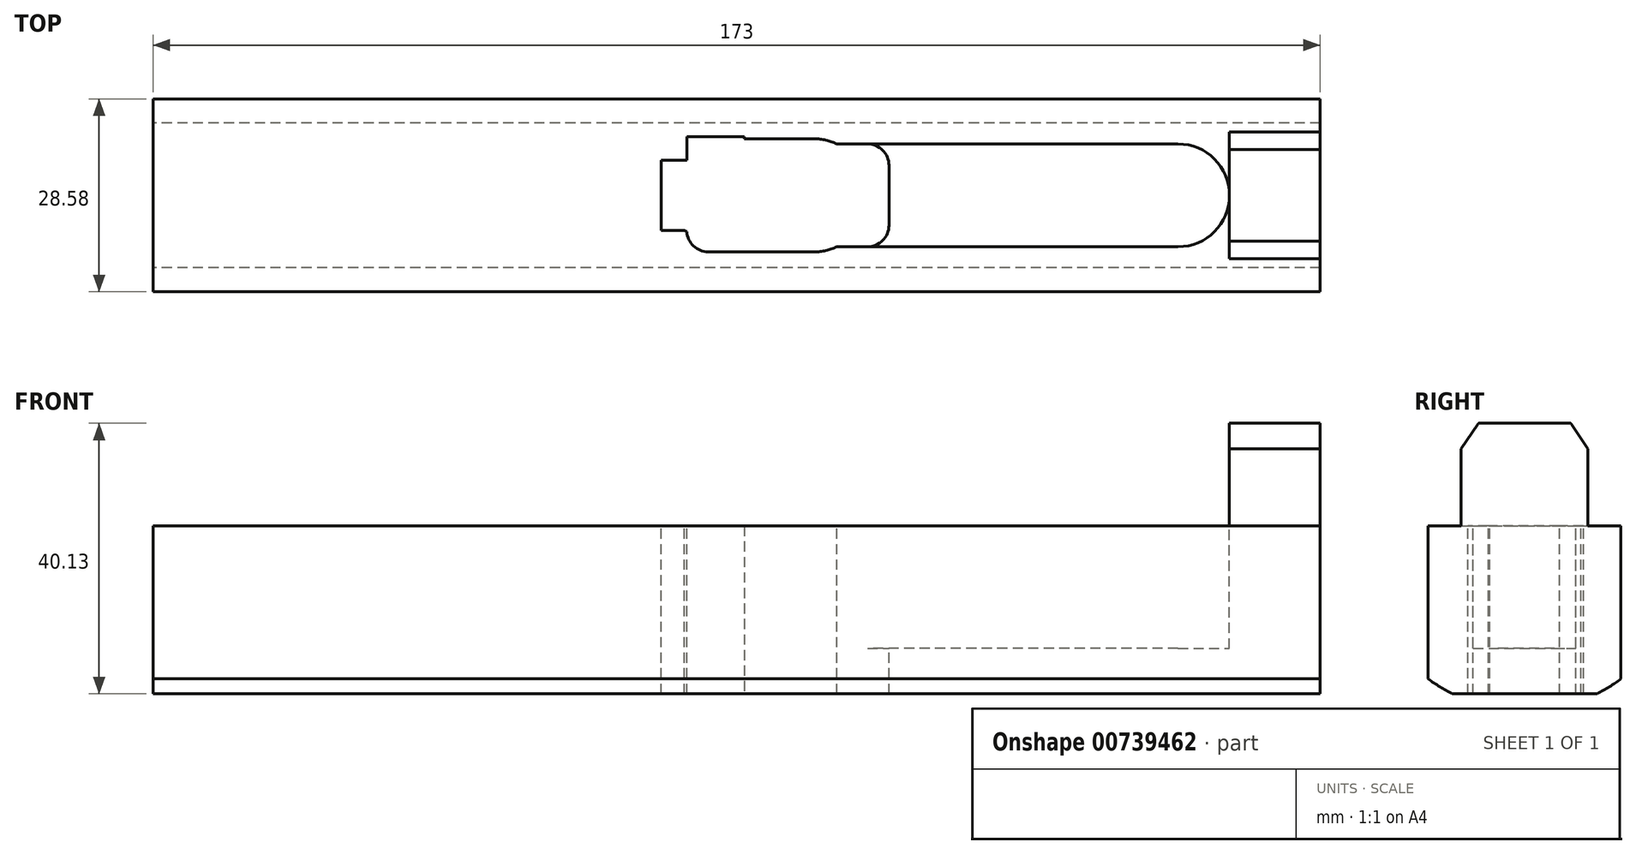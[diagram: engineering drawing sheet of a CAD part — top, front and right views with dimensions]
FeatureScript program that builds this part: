
annotation { "Feature Type Name" : "Feature", "Feature Type Description" : "" }
export const myFeature = defineFeature(function(context is Context, id is Id, definition is map)
    precondition{}
    {
        {
            var Q0;
            Q0=qCreatedBy(makeId("Right.planeOp"),FACE);
            var sketch = newSketch(context, id + "F0", { "sketchPlane" : qUnion([Q0])});
            skLineSegment(sketch, "E0", {"start": v(16, 0) * mm, "end": v(16, 22.54) * mm});
            skLineSegment(sketch, "E1", {"start": v(15.74, 23.38) * mm, "end": v(6.95, 36.34) * mm});
            skLineSegment(sketch, "E2", {"start": v(5.7, 37) * mm, "end": v(-5.7, 37) * mm});
            skLineSegment(sketch, "E3", {"start": v(-6.95, 36.34) * mm, "end": v(-15.74, 23.38) * mm});
            skLineSegment(sketch, "E4", {"start": v(-16, 22.54) * mm, "end": v(-16, 0) * mm});
            skLineSegment(sketch, "E5", {"start": v(-25.86, -6.2) * mm, "end": v(32.15, -6.2) * mm, "construction": true});
            skArc(sketch, "E6", {"start": v(-16, 0) * mm, "mid": v(0, -6.2) * mm, "end": v(16, 0) * mm});
            skPoint(sketch, "E6.third.point", {"position": v(0, -6.2) * mm});
            skPoint(sketch, "E7.visualSharp", {"position": v(-6.5, 37) * mm});
            skArc(sketch, "E7.filletArc", {"start": v(-5.7, 37) * mm, "mid": v(-6.4, 36.83) * mm, "end": v(-6.95, 36.34) * mm});
            skPoint(sketch, "E8.visualSharp", {"position": v(6.5, 37) * mm});
            skArc(sketch, "E8.filletArc", {"start": v(6.95, 36.34) * mm, "mid": v(6.4, 36.83) * mm, "end": v(5.7, 37) * mm});
            skPoint(sketch, "E9.visualSharp", {"position": v(-16, 23) * mm});
            skArc(sketch, "E9.filletArc", {"start": v(-15.74, 23.38) * mm, "mid": v(-15.93, 22.98) * mm, "end": v(-16, 22.54) * mm});
            skPoint(sketch, "E10.visualSharp", {"position": v(16, 23) * mm});
            skArc(sketch, "E10.filletArc", {"start": v(16, 22.54) * mm, "mid": v(15.93, 22.98) * mm, "end": v(15.74, 23.38) * mm});
            skSolve(sketch);
        }
        {
            var Q0;
            Q0 = qSketchRegion(id + "F0", true);
            extrude(context, id + "F1", {"entities" : qUnion([Q0]), "depth" : 173 * mm, "offsetDistance" : 25.4 * mm});
        }
        {
            var Q0;
            Q0=makeQuery(id+"F1.opExtrude","CAP_FACE",FACE,{"disambiguationData":[OSD([sQuery(id+"F0.wireOp",EDGE,"E0"),sQuery(id+"F0.wireOp",EDGE,"E1"),sQuery(id+"F0.wireOp",EDGE,"E2"),sQuery(id+"F0.wireOp",EDGE,"E3"),sQuery(id+"F0.wireOp",EDGE,"E4"),sQuery(id+"F0.wireOp",EDGE,"E6"),sQuery(id+"F0.wireOp",EDGE,"E7.filletArc"),sQuery(id+"F0.wireOp",EDGE,"E8.filletArc"),sQuery(id+"F0.wireOp",EDGE,"E9.filletArc"),sQuery(id+"F0.wireOp",EDGE,"E10.filletArc")])],"isStart":true});
            var sketch = newSketch(context, id + "F2", { "sketchPlane" : qUnion([Q0])});
            skLineSegment(sketch, "E11", {"start": v(-9.4, 21.26) * mm, "end": v(-16, 21.26) * mm});
            skLineSegment(sketch, "E12", {"start": v(-16, 21.26) * mm, "end": v(-16, 39.2) * mm});
            skLineSegment(sketch, "E13", {"start": v(-16, 39.2) * mm, "end": v(16, 39.2) * mm});
            skLineSegment(sketch, "E14", {"start": v(-9.4, 21.26) * mm, "end": v(-9.4, 36.5) * mm});
            skLineSegment(sketch, "E15", {"start": v(-9.4, 36.5) * mm, "end": v(9.4, 36.5) * mm});
            skLineSegment(sketch, "E16", {"start": v(9.4, 36.5) * mm, "end": v(9.4, 21.26) * mm});
            skLineSegment(sketch, "E17", {"start": v(9.4, 21.26) * mm, "end": v(16, 21.26) * mm});
            skLineSegment(sketch, "E18", {"start": v(16, 21.26) * mm, "end": v(16, 39.2) * mm});
            skSolve(sketch);
        }
        {
            var Q0;
            Q0 = qSketchRegion(id + "F2", true);
            extrude(context, id + "F3", {"entities" : qUnion([Q0]), "operationType" : NewBodyOperationType.REMOVE, "endBound" : BoundingType.THROUGH_ALL, "oppositeDirection" : true, "depth" : 25 * mm, "offsetDistance" : 25 * mm});
        }
        {
            var Q0;
            Q0=makeQuery(id+"F1.opExtrude","CAP_FACE",FACE,{"disambiguationData":[OSD([sQuery(id+"F0.wireOp",EDGE,"E0"),sQuery(id+"F0.wireOp",EDGE,"E1"),sQuery(id+"F0.wireOp",EDGE,"E2"),sQuery(id+"F0.wireOp",EDGE,"E3"),sQuery(id+"F0.wireOp",EDGE,"E4"),sQuery(id+"F0.wireOp",EDGE,"E6"),sQuery(id+"F0.wireOp",EDGE,"E7.filletArc"),sQuery(id+"F0.wireOp",EDGE,"E8.filletArc"),sQuery(id+"F0.wireOp",EDGE,"E9.filletArc"),sQuery(id+"F0.wireOp",EDGE,"E10.filletArc")])],"isStart":true});
            var sketch = newSketch(context, id + "F4", { "sketchPlane" : qUnion([Q0])});
            skLineSegment(sketch, "E19", {"start": v(-16, 21.26) * mm, "end": v(-14.29, 21.26) * mm});
            skLineSegment(sketch, "E20", {"start": v(-14.29, 21.26) * mm, "end": v(-14.29, -3.63) * mm});
            skLineSegment(sketch, "E21", {"start": v(-14.29, -3.63) * mm, "end": v(14.29, -3.63) * mm});
            skLineSegment(sketch, "E22", {"start": v(14.29, -3.63) * mm, "end": v(14.29, 21.26) * mm});
            skLineSegment(sketch, "E23", {"start": v(14.29, 21.26) * mm, "end": v(16, 21.26) * mm});
            skLineSegment(sketch, "E24", {"start": v(16, 21.26) * mm, "end": v(16, -10.53) * mm});
            skLineSegment(sketch, "E25", {"start": v(16, -10.53) * mm, "end": v(-16, -10.53) * mm});
            skLineSegment(sketch, "E26", {"start": v(-16, 21.26) * mm, "end": v(-16, -10.53) * mm});
            skSolve(sketch);
        }
        {
            var Q0;
            Q0 = qSketchRegion(id + "F4", true);
            extrude(context, id + "F5", {"entities" : qUnion([Q0]), "operationType" : NewBodyOperationType.REMOVE, "endBound" : BoundingType.THROUGH_ALL, "oppositeDirection" : true, "depth" : 25 * mm, "offsetDistance" : 25 * mm});
        }
        {
            var Q0;
            Q0=makeQuery(id+"F3.boolean.opBoolean","COPY",FACE,{"derivedFrom":makeQuery(id+"F3.opExtrude","SWEPT_FACE",FACE,{"disambiguationData":[OSD([sQuery(id+"F2.wireOp",EDGE,"E14")])]})});
            var sketch = newSketch(context, id + "F6", { "sketchPlane" : qUnion([Q0])});
            skLineSegment(sketch, "E27.bottom", {"start": v(-159.54, 21.26) * mm, "end": v(0, 21.26) * mm});
            skLineSegment(sketch, "E27.top", {"start": v(-159.54, 36.5) * mm, "end": v(0, 36.5) * mm});
            skLineSegment(sketch, "E27.left", {"start": v(-159.54, 21.26) * mm, "end": v(-159.54, 36.5) * mm});
            skLineSegment(sketch, "E27.right", {"start": v(0, 21.26) * mm, "end": v(0, 36.5) * mm});
            skSolve(sketch);
        }
        {
            var Q0;
            Q0 = qSketchRegion(id + "F6", true);
            extrude(context, id + "F7", {"entities" : qUnion([Q0]), "operationType" : NewBodyOperationType.REMOVE, "endBound" : BoundingType.THROUGH_ALL, "oppositeDirection" : true, "depth" : 25 * mm, "offsetDistance" : 25 * mm});
        }
        {
            var Q0;
            Q0=makeQuery(id+"F7.boolean.opBoolean","MERGE",FACE,{"derivedFrom":[makeQuery(id+"F3.boolean.opBoolean","COPY",FACE,{"derivedFrom":makeQuery(id+"F3.opExtrude","SWEPT_FACE",FACE,{"disambiguationData":[OSD([sQuery(id+"F2.wireOp",EDGE,"E11")])]})}),makeQuery(id+"F3.boolean.opBoolean","COPY",FACE,{"derivedFrom":makeQuery(id+"F3.opExtrude","SWEPT_FACE",FACE,{"disambiguationData":[OSD([sQuery(id+"F2.wireOp",EDGE,"E17")])]})}),makeQuery(id+"F7.opExtrude","SWEPT_FACE",FACE,{"disambiguationData":[OSD([sQuery(id+"F6.wireOp",EDGE,"E27.bottom")])]})]});
            var sketch = newSketch(context, id + "F8", { "sketchPlane" : qUnion([Q0])});
            skArc(sketch, "E28", {"start": v(151.92, -7.62) * mm, "mid": v(159.54, 0) * mm, "end": v(151.92, 7.62) * mm});
            skLineSegment(sketch, "E29", {"start": v(151.92, 7.62) * mm, "end": v(85.98, 7.62) * mm});
            skLineSegment(sketch, "E30", {"start": v(151.92, -7.62) * mm, "end": v(85.98, -7.62) * mm});
            skArc(sketch, "E31", {"start": v(85.98, 7.62) * mm, "mid": v(78.36, 0) * mm, "end": v(85.98, -7.62) * mm});
            skSolve(sketch);
        }
        {
            var Q0;
            Q0 = qSketchRegion(id + "F8", true);
            extrude(context, id + "F9", {"entities" : qUnion([Q0]), "operationType" : NewBodyOperationType.REMOVE, "oppositeDirection" : true, "depth" : 18.16 * mm, "offsetDistance" : 25 * mm});
        }
        {
            var Q0;
            Q0=makeQuery(id+"F7.boolean.opBoolean","MERGE",FACE,{"derivedFrom":[makeQuery(id+"F3.boolean.opBoolean","COPY",FACE,{"derivedFrom":makeQuery(id+"F3.opExtrude","SWEPT_FACE",FACE,{"disambiguationData":[OSD([sQuery(id+"F2.wireOp",EDGE,"E11")])]})}),makeQuery(id+"F3.boolean.opBoolean","COPY",FACE,{"derivedFrom":makeQuery(id+"F3.opExtrude","SWEPT_FACE",FACE,{"disambiguationData":[OSD([sQuery(id+"F2.wireOp",EDGE,"E17")])]})}),makeQuery(id+"F7.opExtrude","SWEPT_FACE",FACE,{"disambiguationData":[OSD([sQuery(id+"F6.wireOp",EDGE,"E27.bottom")])]})]});
            var sketch = newSketch(context, id + "F10", { "sketchPlane" : qUnion([Q0])});
            skLineSegment(sketch, "E32", {"start": v(109.07, 4.44) * mm, "end": v(109.07, -4.45) * mm});
            skLineSegment(sketch, "E33", {"start": v(105.9, -7.62) * mm, "end": v(101.34, -7.62) * mm});
            skLineSegment(sketch, "E34", {"start": v(98.02, -8.38) * mm, "end": v(82.27, -8.38) * mm});
            skLineSegment(sketch, "E35", {"start": v(105.9, 7.62) * mm, "end": v(101.34, 7.62) * mm});
            skLineSegment(sketch, "E36", {"start": v(98.02, 8.38) * mm, "end": v(79.86, 8.38) * mm});
            skArc(sketch, "E37", {"start": v(101.34, 7.62) * mm, "mid": v(99.72, 8.19) * mm, "end": v(98.02, 8.38) * mm});
            skArc(sketch, "E38", {"start": v(98.02, -8.38) * mm, "mid": v(99.72, -8.19) * mm, "end": v(101.34, -7.62) * mm});
            skArc(sketch, "E39.filletArc", {"start": v(109.07, 4.44) * mm, "mid": v(108.14, 6.7) * mm, "end": v(105.9, 7.62) * mm});
            skArc(sketch, "E40.filletArc", {"start": v(105.9, -7.62) * mm, "mid": v(108.14, -6.7) * mm, "end": v(109.07, -4.45) * mm});
            skLineSegment(sketch, "E41", {"start": v(75.8, 5) * mm, "end": v(75.8, -1.64) * mm});
            skArc(sketch, "E42.filletArc", {"start": v(79.1, -5.38) * mm, "mid": v(80.09, -7.51) * mm, "end": v(82.27, -8.38) * mm});
            skLineSegment(sketch, "E43", {"start": v(77.38, -4.4) * mm, "end": v(79.1, -5.38) * mm});
            skArc(sketch, "E44.filletArc", {"start": v(75.8, -1.64) * mm, "mid": v(76.22, -3.23) * mm, "end": v(77.38, -4.4) * mm});
            skLineSegment(sketch, "E45", {"start": v(75.8, 5) * mm, "end": v(79.86, 5) * mm});
            skLineSegment(sketch, "E46", {"start": v(79.86, 5) * mm, "end": v(79.86, 8.38) * mm});
            skSolve(sketch);
        }
        {
            var Q0;
            Q0 = qSketchRegion(id + "F10", true);
            extrude(context, id + "F11", {"entities" : qUnion([Q0]), "operationType" : NewBodyOperationType.REMOVE, "endBound" : BoundingType.THROUGH_ALL, "oppositeDirection" : true, "depth" : 25 * mm, "offsetDistance" : 25 * mm});
        }
        {
            var Q0;
            Q0=makeQuery(id+"F7.boolean.opBoolean","MERGE",FACE,{"derivedFrom":[makeQuery(id+"F3.boolean.opBoolean","COPY",FACE,{"derivedFrom":makeQuery(id+"F3.opExtrude","SWEPT_FACE",FACE,{"disambiguationData":[OSD([sQuery(id+"F2.wireOp",EDGE,"E11")])]})}),makeQuery(id+"F3.boolean.opBoolean","COPY",FACE,{"derivedFrom":makeQuery(id+"F3.opExtrude","SWEPT_FACE",FACE,{"disambiguationData":[OSD([sQuery(id+"F2.wireOp",EDGE,"E17")])]})}),makeQuery(id+"F7.opExtrude","SWEPT_FACE",FACE,{"disambiguationData":[OSD([sQuery(id+"F6.wireOp",EDGE,"E27.bottom")])]})]});
            var sketch = newSketch(context, id + "F12", { "sketchPlane" : qUnion([Q0])});
            skLineSegment(sketch, "E47", {"start": v(87.6, -5.18) * mm, "end": v(87.6, 8.7) * mm});
            skLineSegment(sketch, "E48", {"start": v(87.6, 8.7) * mm, "end": v(79.1, 8.7) * mm});
            skLineSegment(sketch, "E49", {"start": v(79.1, 8.7) * mm, "end": v(79.1, 5.18) * mm});
            skLineSegment(sketch, "E50", {"start": v(79.1, 5.18) * mm, "end": v(75.31, 5.18) * mm});
            skLineSegment(sketch, "E51", {"start": v(75.31, 5.18) * mm, "end": v(75.31, -5.18) * mm});
            skLineSegment(sketch, "E52", {"start": v(75.31, -5.18) * mm, "end": v(87.6, -5.18) * mm});
            skSolve(sketch);
        }
        {
            var Q0;
            Q0 = qSketchRegion(id + "F12", true);
            extrude(context, id + "F13", {"entities" : qUnion([Q0]), "operationType" : NewBodyOperationType.REMOVE, "endBound" : BoundingType.THROUGH_ALL, "oppositeDirection" : true, "depth" : 25 * mm, "offsetDistance" : 25 * mm});
        }
    });
